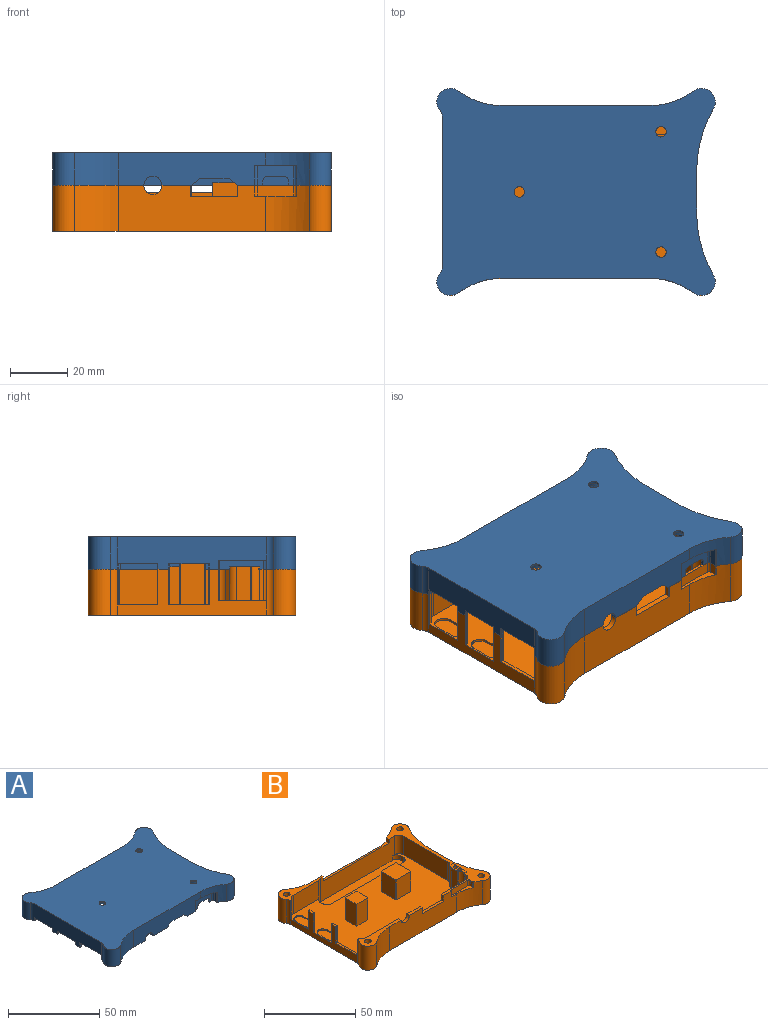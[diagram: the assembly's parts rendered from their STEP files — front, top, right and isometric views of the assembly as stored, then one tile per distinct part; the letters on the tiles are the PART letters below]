
ASSEMBLY  parts=2 mates=1
PART A: 96 faces, bbox 97.3x72.4x11.4 mm
  f0: cylinder r=1.6mm len=1.6mm, axis (0,-1,0), area 2.4mm2, adj f1,f2,f45,f55
  f1: plane 1.58x0.96mm, normal (1,0,0), area 1.5mm2, adj f0,f45,f55,f72
  f2: plane 5.69x0.96mm, normal (0,0,-1), area 5.5mm2, adj f0,f45,f47,f55
  f3: plane 11.74x2.84mm, normal (1,0,0), area 33.4mm2, adj f6,f8,f11,f71
  f4: plane 11.49x2.84mm, normal (0,-1,0), area 32.7mm2, adj f5,f6,f8,f71
  f5: cylinder r=0.25mm len=2.85mm, axis (0,0,1), area 1.1mm2, adj f4,f6,f7,f71
  f6: plane 12.25x12mm, normal (0,0,-1), area 146.9mm2, adj f3,f4,f5,f7,f8,f9,f10,f11
  f7: plane 11.74x2.84mm, normal (-1,0,0), area 33.4mm2, adj f5,f6,f9,f71
  f8: cylinder r=0.25mm len=2.85mm, axis (0,0,1), area 1.1mm2, adj f3,f4,f6,f71
  f9: cylinder r=0.25mm len=2.85mm, axis (0,0,1), area 1.1mm2, adj f6,f7,f10,f71
  f10: plane 11.49x2.84mm, normal (0,1,0), area 32.7mm2, adj f6,f9,f11,f71
  f11: cylinder r=0.25mm len=2.85mm, axis (0,0,1), area 1.1mm2, adj f3,f6,f10,f71
  f12: cylinder r=0.25mm len=2.03mm, axis (0,0,1), area 0.8mm2, adj f19,f57,f94,f95
  f13: cylinder r=0.23mm len=2.03mm, axis (0,0,-1), area 0.6mm2, adj f19,f43,f69,f70
  f14: cylinder r=3.43mm len=11.43mm, axis (0,0,-1), area 27.9mm2, adj f20,f25,f38,f70,f92
  f15: plane 16.88x1.44mm, normal (0,0,-1), area 19.7mm2, adj f16,f17,f18,f37,f44,f57,f66,f67
  f16: cylinder r=0.25mm len=3.23mm, axis (0,0,1), area 1.3mm2, adj f15,f17,f57,f65
  f17: plane 3.23x0.69mm, normal (0,-1,0), area 2.2mm2, adj f15,f16,f18,f65
  f18: cylinder r=0.25mm len=3.23mm, axis (0,0,1), area 1.3mm2, adj f15,f17,f65,f92
  f19: plane 14.2x1.4mm, normal (0,0,-1), area 16.5mm2, adj f12,f13,f20,f43,f57,f69,f92,f93
  f20: cylinder r=0.23mm len=2.03mm, axis (0,0,-1), area 0.7mm2, adj f14,f19,f69,f70
  f21: cylinder r=1.83mm len=3.66mm, axis (0,0,1), area 9mm2, adj f24,f38
  f22: cylinder r=1.83mm len=3.66mm, axis (0,0,1), area 9mm2, adj f23,f38
  f23: cone r=1.83mm half-angle=41deg, axis (0,0,-1), area 63.9mm2, adj f22,f71
  f24: cone r=1.77mm half-angle=41deg, axis (0,0,-1), area 63.9mm2, adj f21,f71
  f25: cylinder r=4.76mm len=11.43mm, axis (0,0,-1), area 159.2mm2, adj f14,f26,f38,f70
  f26: cylinder r=25.4mm len=15.24mm, axis (0,0,-1), area 186.8mm2, adj f25,f27,f38,f70
  f27: plane 51.56x11.43mm, normal (0,1,0), area 589.4mm2, adj f26,f28,f38,f70
  f28: cylinder r=25.4mm len=15.24mm, axis (0,0,-1), area 186.8mm2, adj f27,f29,f38,f70
  f29: cylinder r=4.76mm len=11.43mm, axis (0,0,-1), area 148.8mm2, adj f28,f30,f38,f70
  f30: cylinder r=44.45mm len=22.05mm, axis (0,0,-1), area 263.7mm2, adj f29,f31,f38,f70
  f31: plane 14.04x11.43mm, normal (1,0,0), area 140.5mm2, adj f30,f32,f38,f70,f80,f81,f82,f83
  f32: cylinder r=44.45mm len=22.05mm, axis (0,0,-1), area 263.7mm2, adj f31,f33,f38,f70
  f33: cylinder r=4.76mm len=11.43mm, axis (0,0,-1), area 148.8mm2, adj f32,f34,f38,f70
  f34: cylinder r=25.4mm len=15.24mm, axis (0,0,-1), area 108.6mm2, adj f33,f38,f46,f51,f52,f70
  f35: cylinder r=25.4mm len=15.24mm, axis (0,0,-1), area 186.8mm2, adj f36,f38,f46,f49
  f36: cylinder r=4.76mm len=11.43mm, axis (0,0,-1), area 159.2mm2, adj f35,f37,f38,f49
  f37: cylinder r=3.43mm len=11.43mm, axis (0,0,-1), area 27.5mm2, adj f15,f36,f38,f49,f66,f92
  f38: plane 97.28x72.39mm, normal (0,0,1), area 5689.1mm2, adj f14,f21,f22,f25,f26,f27,f28,f29
  f39: cylinder r=3.43mm len=8.05mm, axis (0,0,1), area 43.4mm2, adj f40,f45,f70,f71
  f40: plane 49.66x8.05mm, normal (-1,0,0), area 379.9mm2, adj f39,f41,f70,f71,f80,f81,f82,f83
  f41: cylinder r=3.43mm len=8.05mm, axis (0,0,1), area 43.4mm2, adj f40,f42,f70,f71
  f42: plane 78.74x8.05mm, normal (0,-1,0), area 634mm2, adj f41,f43,f70,f71
  f43: cylinder r=3.43mm len=8.05mm, axis (0,0,1), area 40.9mm2, adj f13,f19,f42,f57,f70,f71
  f44: cylinder r=3.43mm len=8.05mm, axis (0,0,1), area 39.2mm2, adj f15,f45,f49,f57,f68,f71
  f45: plane 78.74x8.05mm, normal (0,1,0), area 558.8mm2, adj f0,f1,f2,f39,f44,f47,f48,f49
  f46: plane 51.56x11.43mm, normal (0,-1,0), area 513.2mm2, adj f34,f35,f38,f49,f50,f51,f72,f73
  f47: cylinder r=1.6mm len=1.6mm, axis (0,-1,0), area 2.4mm2, adj f2,f45,f48,f55
  f48: plane 1.58x0.96mm, normal (-1,0,0), area 1.5mm2, adj f45,f47,f55,f70
  f49: plane 31.8x10.25mm, normal (0,0,-1), area 122.7mm2, adj f35,f36,f37,f44,f45,f46,f66,f67
  f50: cylinder r=0.25mm len=6.99mm, axis (0,0,1), area 2.5mm2, adj f46,f51,f56,f72
  f51: plane 14.86x3.37mm, normal (0,0,-1), area 21.6mm2, adj f34,f46,f50,f52,f53,f54,f55,f56
  f52: cylinder r=0.25mm len=6.99mm, axis (0,0,1), area 2mm2, adj f34,f51,f53,f70
  f53: plane 6.99x2.25mm, normal (-1,0,0), area 15.7mm2, adj f51,f52,f54,f70
  f54: cylinder r=0.89mm len=6.99mm, axis (0,0,1), area 9.8mm2, adj f51,f53,f55,f70
  f55: plane 12.7x6.99mm, normal (0,-1,0), area 61.6mm2, adj f0,f1,f2,f47,f48,f51,f54,f56
  f56: cylinder r=0.89mm len=6.99mm, axis (0,0,1), area 8.7mm2, adj f50,f51,f55,f72
  f57: plane 49.66x8.05mm, normal (1,0,0), area 294.6mm2, adj f12,f15,f16,f19,f43,f44,f60,f61
  f58: cylinder r=0.25mm len=2.03mm, axis (0,0,1), area 0.8mm2, adj f59,f61,f65,f92
  f59: plane 2.03x0.69mm, normal (0,1,0), area 1.4mm2, adj f58,f60,f61,f65
  f60: cylinder r=0.25mm len=2.03mm, axis (0,0,1), area 0.8mm2, adj f57,f59,f61,f65
  f61: plane 14.22x1.19mm, normal (0,0,-1), area 16.4mm2, adj f57,f58,f59,f60,f62,f63,f64,f92
  f62: cylinder r=0.25mm len=2.03mm, axis (0,0,1), area 0.8mm2, adj f57,f61,f63,f95
  f63: plane 2.03x0.69mm, normal (0,-1,0), area 1.4mm2, adj f61,f62,f64,f95
  f64: cylinder r=0.25mm len=2.03mm, axis (0,0,1), area 0.8mm2, adj f61,f63,f92,f95
  f65: plane 3.7x1.19mm, normal (0,0,-1), area 4.4mm2, adj f16,f17,f18,f57,f58,f59,f60,f92
  f66: cylinder r=0.25mm len=3.23mm, axis (0,0,1), area 1.3mm2, adj f15,f37,f49,f67
  f67: plane 3.23x0.95mm, normal (0,1,0), area 3.1mm2, adj f15,f49,f66,f68
  f68: cylinder r=0.25mm len=3.23mm, axis (0,0,1), area 1mm2, adj f15,f44,f49,f67
  f69: plane 2.03x0.96mm, normal (0,-1,0), area 1.9mm2, adj f13,f19,f20,f70
  f70: plane 97.28x72.39mm, normal (0,0,-1), area 572.3mm2, adj f13,f14,f20,f25,f26,f27,f28,f29
  f71: plane 85.6x56.52mm, normal (0,0,-1), area 4523.3mm2, adj f3,f4,f5,f7,f8,f9,f10,f11
  f72: plane 9.02x1.91mm, normal (0,0,-1), area 14.7mm2, adj f1,f45,f46,f50,f55,f56,f75
  f73: cylinder r=3.17mm len=6.35mm, axis (0,1,0), area 19mm2, adj f45,f46,f49,f74
  f74: plane 10.39x1.91mm, normal (0,0,-1), area 19.8mm2, adj f45,f46,f73,f77
  f75: plane 3.18x2.54mm, normal (-0.62,0,-0.78), area 7.7mm2, adj f45,f46,f72,f76
  f76: plane 9.53x1.91mm, normal (0,0,-1), area 18.1mm2, adj f45,f46,f75,f77
  f77: plane 3.18x2.54mm, normal (0.62,0,-0.78), area 7.7mm2, adj f45,f46,f74,f76
  f78: cylinder r=1.83mm len=3.66mm, axis (0,0,1), area 9mm2, adj f38,f79
  f79: cone r=1.83mm half-angle=41deg, axis (0,0,-1), area 63.9mm2, adj f71,f78
  f80: cylinder r=0.81mm len=2.03mm, axis (1,0,0), area 5.2mm2, adj f31,f40,f81,f83
  f81: plane 11x2.03mm, normal (0,0,-1), area 22.3mm2, adj f31,f40,f80,f82
  f82: cylinder r=0.81mm len=2.03mm, axis (1,0,0), area 5.2mm2, adj f31,f40,f81,f83
  f83: plane 11x2.03mm, normal (0,0,1), area 22.3mm2, adj f31,f40,f80,f82
  f84: cylinder r=1.52mm len=9.88mm, axis (0,0,1), area 94.6mm2, adj f49,f90
  f85: cylinder r=1.52mm len=9.88mm, axis (0,0,1), area 94.6mm2, adj f70,f91
  f86: cylinder r=1.52mm len=9.88mm, axis (0,0,1), area 94.6mm2, adj f70,f88
  f87: cylinder r=1.52mm len=9.88mm, axis (0,0,1), area 94.6mm2, adj f70,f89
  f88: cone r=0.8mm half-angle=59deg, axis (0,0,-1), area 8.5mm2, adj f86
  f89: cone r=0.8mm half-angle=59deg, axis (0,0,-1), area 8.5mm2, adj f87
  f90: cone r=0.8mm half-angle=59deg, axis (0,0,-1), area 8.5mm2, adj f84
  f91: cone r=0.8mm half-angle=59deg, axis (0,0,-1), area 8.5mm2, adj f85
  f92: plane 52.18x11.43mm, normal (-1,0,0), area 484.5mm2, adj f14,f15,f18,f19,f37,f38,f58,f61
  f93: cylinder r=0.25mm len=2.03mm, axis (0,0,-1), area 0.8mm2, adj f19,f92,f94,f95
  f94: plane 2.03x0.69mm, normal (0,1,0), area 1.4mm2, adj f12,f19,f93,f95
  f95: plane 4.28x1.19mm, normal (0,0,-1), area 5.1mm2, adj f12,f57,f62,f63,f64,f92,f93,f94
PART B: 132 faces, bbox 97.3x72.4x18.3 mm
  f0: cylinder r=0.23mm len=12.45mm, axis (0,0,1), area 4.5mm2, adj f21,f36,f65,f92
  f1: cylinder r=0.25mm len=0.94mm, axis (0,0,-1), area 0.4mm2, adj f28,f41,f56,f83
  f2: cylinder r=3.43mm len=12.45mm, axis (0,0,-1), area 33.8mm2, adj f28,f36,f51,f101
  f3: plane 50.8x2.31mm, normal (0,0,1), area 70.5mm2, adj f9,f12,f24,f37,f127
  f4: cylinder r=3.17mm len=6.35mm, axis (0,-1,0), area 19mm2, adj f42,f43,f88,f105
  f5: cylinder r=0.25mm len=3.81mm, axis (0,0,-1), area 1.1mm2, adj f28,f29,f31,f81
  f6: cylinder r=0.25mm len=10.92mm, axis (0,0,-1), area 4.4mm2, adj f15,f66,f93,f94
  f7: cylinder r=0.25mm len=3.94mm, axis (0,0,1), area 1.6mm2, adj f43,f70,f96,f105
  f8: plane 6.86x0.76mm, normal (1,0,0), area 5.2mm2, adj f35,f36,f47,f86
  f9: cylinder r=25.4mm len=16.08mm, axis (0,0,1), area 244.9mm2, adj f3,f12,f28,f62,f85,f127
  f10: cylinder r=0.25mm len=3.81mm, axis (0,0,-1), area 1.3mm2, adj f11,f28,f29,f88
  f11: cylinder r=0.89mm len=3.81mm, axis (0,0,-1), area 4.7mm2, adj f10,f28,f29,f50
  f12: plane 51.56x16.08mm, normal (0,1,0), area 717.7mm2, adj f3,f9,f37,f85,f92,f126
  f13: plane 2.12x0.94mm, normal (0,1,0), area 2mm2, adj f28,f57,f83,f103
  f14: plane 52.18x16.08mm, normal (-1,0,0), area 301.9mm2, adj f36,f64,f65,f67,f69,f76,f85,f93
  f15: plane 18.72x12.45mm, normal (1,0,0), area 63.4mm2, adj f6,f23,f33,f36,f93,f94
  f16: cylinder r=4.76mm len=16.08mm, axis (0,0,1), area 209.3mm2, adj f28,f81,f85,f87
  f17: plane 12.45x0.69mm, normal (0,1,0), area 8.5mm2, adj f23,f36,f64,f93
  f18: cylinder r=0.89mm len=3.81mm, axis (0,0,-1), area 5.3mm2, adj f28,f29,f31,f50
  f19: plane 13.39x4.89mm, normal (-1,0,0), area 65.4mm2, adj f36,f52,f63,f83
  f20: cylinder r=3.43mm len=3.43mm, axis (0,0,-1), area 16.6mm2, adj f36,f38,f84,f129
  f21: plane 12.45x0.96mm, normal (0,-1,0), area 11.9mm2, adj f0,f36,f92,f131
  f22: plane 3.07x1.78mm, normal (-1,0,0), area 5.5mm2, adj f36,f38,f48,f49
  f23: cylinder r=0.25mm len=12.45mm, axis (0,0,-1), area 5mm2, adj f15,f17,f36,f93
  f24: plane 57.06x15.52mm, normal (0,-1,0), area 751.3mm2, adj f3,f28,f34,f36,f37,f38,f48,f92
  f25: cylinder r=0.25mm len=3.94mm, axis (0,0,-1), area 1.6mm2, adj f28,f68,f70,f88
  f26: cylinder r=3.43mm len=12.45mm, axis (0,0,-1), area 67mm2, adj f28,f36,f72,f105
  f27: cylinder r=0.25mm len=0.94mm, axis (0,0,-1), area 0.4mm2, adj f28,f41,f83,f102
  f28: plane 72.39x32.87mm, normal (0,0,1), area 376.6mm2, adj f1,f2,f5,f9,f10,f11,f13,f16
  f29: plane 14.86x3.37mm, normal (0,0,1), area 21.6mm2, adj f5,f10,f11,f18,f31,f50,f81,f88
  f30: cylinder r=44.45mm len=22.05mm, axis (0,0,1), area 371mm2, adj f28,f62,f71,f85
  f31: plane 3.81x2.25mm, normal (-1,0,0), area 8.6mm2, adj f5,f18,f28,f29
  f32: cylinder r=1.83mm len=13.48mm, axis (0,0,-1), area 154.9mm2, adj f42,f90
  f33: cylinder r=3.43mm len=12.45mm, axis (0,0,1), area 53mm2, adj f15,f36,f42,f94,f95,f105
  f34: cylinder r=3.43mm len=12.45mm, axis (0,0,1), area 67mm2, adj f24,f28,f36,f51
  f35: cylinder r=3.17mm len=6.35mm, axis (0,0,-1), area 7.6mm2, adj f8,f36,f47,f55
  f36: plane 86.79x57.08mm, normal (0,0,1), area 3958.8mm2, adj f0,f2,f8,f14,f15,f17,f19,f20
  f37: plane 2.54x1.34mm, normal (1,0,0), area 3.4mm2, adj f3,f12,f24,f92
  f38: plane 62.23x8.64mm, normal (0,0,1), area 527.3mm2, adj f20,f22,f24,f48,f49,f84,f129,f130
  f39: plane 10.92x1.07mm, normal (0,1,0), area 11.7mm2, adj f42,f78,f94,f95
  f40: plane 12.45x3.78mm, normal (1,0,0), area 47mm2, adj f36,f59,f98,f100
  f41: plane 1.18x0.94mm, normal (0,-1,0), area 1.1mm2, adj f1,f27,f28,f83
  f42: plane 31.8x10.25mm, normal (0,0,1), area 119.5mm2, adj f4,f32,f33,f39,f45,f69,f78,f80
  f43: plane 10.39x1.91mm, normal (0,0,1), area 19.8mm2, adj f4,f7,f77,f88,f96,f105
  f44: cylinder r=0.25mm len=3.94mm, axis (0,0,-1), area 1.6mm2, adj f28,f68,f70,f105
  f45: cylinder r=4.76mm len=16.08mm, axis (0,0,1), area 224mm2, adj f42,f69,f80,f85
  f46: cylinder r=1.1mm len=17.02mm, axis (0,0,1), area 118.1mm2, adj f83,f85
  f47: plane 13.21x6.35mm, normal (0,0,1), area 75.2mm2, adj f8,f35,f55,f86
  f48: cylinder r=3.43mm len=3.43mm, axis (0,0,-1), area 16.6mm2, adj f22,f24,f36,f38
  f49: cylinder r=3.43mm len=3.43mm, axis (0,0,-1), area 16.6mm2, adj f22,f36,f38,f129
  f50: plane 12.7x3.81mm, normal (0,-1,0), area 48.4mm2, adj f11,f18,f28,f29
  f51: plane 34.64x12.45mm, normal (-1,0,0), area 431.2mm2, adj f2,f28,f34,f36
  f52: cylinder r=3.43mm len=13.39mm, axis (0,0,-1), area 36.2mm2, adj f19,f28,f36,f57,f83,f101
  f53: plane 13.21x6.35mm, normal (0,0,1), area 75.2mm2, adj f54,f58,f74,f104
  f54: cylinder r=3.17mm len=6.35mm, axis (0,0,-1), area 7.6mm2, adj f36,f53,f58,f104
  f55: plane 6.86x0.76mm, normal (-1,0,0), area 5.2mm2, adj f35,f36,f47,f86
  f56: plane 9.97x0.94mm, normal (1,0,0), area 9.4mm2, adj f1,f28,f83,f103
  f57: cylinder r=0.25mm len=0.94mm, axis (0,0,-1), area 0.2mm2, adj f13,f28,f52,f83
  f58: plane 6.86x0.76mm, normal (1,0,0), area 5.2mm2, adj f36,f53,f54,f74
  f59: cylinder r=0.25mm len=12.45mm, axis (0,0,-1), area 5mm2, adj f36,f40,f97,f98
  f60: cylinder r=1.1mm len=17.02mm, axis (0,0,1), area 118.1mm2, adj f83,f85
  f61: cone r=1.83mm half-angle=41deg, axis (0,0,-1), area 63.9mm2, adj f85,f125
  f62: cylinder r=4.76mm len=16.08mm, axis (0,0,1), area 209.3mm2, adj f9,f28,f30,f85
  f63: cylinder r=0.25mm len=13.39mm, axis (0,0,-1), area 3.5mm2, adj f19,f36,f83,f102
  f64: cylinder r=0.25mm len=12.45mm, axis (0,0,-1), area 5mm2, adj f14,f17,f36,f93
  f65: cylinder r=3.43mm len=16.08mm, axis (0,0,1), area 39.2mm2, adj f0,f14,f75,f85,f92
  f66: plane 10.92x0.69mm, normal (0,-1,0), area 7.5mm2, adj f6,f67,f93,f94
  f67: cylinder r=0.25mm len=10.92mm, axis (0,0,-1), area 4.4mm2, adj f14,f66,f93,f94
  f68: plane 3.94x1.4mm, normal (-1,0,0), area 5.5mm2, adj f25,f28,f44,f70
  f69: cylinder r=3.43mm len=16.08mm, axis (0,0,1), area 39.1mm2, adj f14,f42,f45,f78,f85
  f70: plane 16.38x1.91mm, normal (0,0,1), area 30.3mm2, adj f7,f25,f44,f68,f77,f88,f96,f105
  f71: plane 16.08x14.04mm, normal (1,0,0), area 225.7mm2, adj f28,f30,f85,f87
  f72: plane 12.45x1.22mm, normal (-1,0,0), area 15.2mm2, adj f26,f28,f36,f102
  f73: cylinder r=3.43mm len=12.45mm, axis (0,0,-1), area 52.1mm2, adj f36,f92,f128,f131
  f74: cylinder r=3.17mm len=6.35mm, axis (0,0,-1), area 7.6mm2, adj f36,f53,f58,f104
  f75: cylinder r=4.76mm len=16.08mm, axis (0,0,1), area 224mm2, adj f65,f85,f92,f126
  f76: cylinder r=0.25mm len=12.45mm, axis (0,0,-1), area 5mm2, adj f14,f36,f97,f98
  f77: cylinder r=0.25mm len=3.94mm, axis (0,0,1), area 1.6mm2, adj f43,f70,f88,f96
  f78: cylinder r=0.15mm len=10.92mm, axis (0,0,-1), area 2.6mm2, adj f39,f42,f69,f94
  f79: cylinder r=1.83mm len=13.48mm, axis (0,0,-1), area 154.9mm2, adj f28,f124
  f80: cylinder r=25.4mm len=16.08mm, axis (0,0,1), area 262.8mm2, adj f42,f45,f85,f88
  f81: cylinder r=25.4mm len=16.08mm, axis (0,0,1), area 220.1mm2, adj f5,f16,f28,f29,f85,f88
  f82: plane 12.45x0.69mm, normal (0,1,0), area 8.5mm2, adj f36,f98,f99,f100
  f83: plane 10.48x3.48mm, normal (0,0,1), area 24.2mm2, adj f1,f13,f19,f27,f41,f46,f52,f56
  f84: plane 3.07x1.78mm, normal (1,0,0), area 5.5mm2, adj f20,f36,f38,f130
  f85: plane 97.28x72.39mm, normal (0,0,-1), area 5503.1mm2, adj f9,f12,f14,f16,f30,f45,f46,f60
  f86: cylinder r=3.17mm len=6.35mm, axis (0,0,-1), area 7.6mm2, adj f8,f36,f47,f55
  f87: cylinder r=44.45mm len=22.05mm, axis (0,0,1), area 371mm2, adj f16,f28,f71,f85
  f88: plane 51.56x16.08mm, normal (0,-1,0), area 733.4mm2, adj f4,f10,f25,f28,f29,f42,f43,f70
  f89: cylinder r=1.83mm len=13.48mm, axis (0,0,-1), area 154.9mm2, adj f91,f92
  f90: cone r=1.83mm half-angle=41deg, axis (0,0,-1), area 63.9mm2, adj f32,f85
  f91: cone r=1.83mm half-angle=41deg, axis (0,0,-1), area 64.1mm2, adj f85,f89
  f92: plane 30.57x10.34mm, normal (0,0,1), area 115.3mm2, adj f0,f12,f21,f24,f37,f65,f73,f75
  f93: plane 3.7x1.19mm, normal (0,0,1), area 4.4mm2, adj f6,f14,f15,f17,f23,f64,f66,f67
  f94: plane 16.79x1.43mm, normal (0,0,1), area 19.7mm2, adj f6,f14,f15,f33,f39,f66,f67,f78
  f95: cylinder r=0.23mm len=10.92mm, axis (0,0,1), area 3mm2, adj f33,f39,f42,f94
  f96: plane 3.94x1.4mm, normal (1,0,0), area 5.5mm2, adj f7,f43,f70,f77
  f97: plane 12.45x0.69mm, normal (0,-1,0), area 8.5mm2, adj f36,f59,f76,f98
  f98: plane 4.28x1.19mm, normal (0,0,1), area 5.1mm2, adj f14,f40,f59,f76,f82,f97,f99,f100
  f99: cylinder r=0.25mm len=12.45mm, axis (0,0,1), area 5mm2, adj f14,f36,f82,f98
  f100: cylinder r=0.25mm len=12.45mm, axis (0,0,-1), area 5mm2, adj f36,f40,f82,f98
  f101: plane 12.45x1.44mm, normal (-0.7,0.71,0), area 25.2mm2, adj f2,f28,f36,f52
  f102: cylinder r=3.43mm len=13.39mm, axis (0,0,-1), area 47.2mm2, adj f27,f28,f36,f63,f72,f83
  f103: cylinder r=0.25mm len=0.94mm, axis (0,0,-1), area 0.4mm2, adj f13,f28,f56,f83
  f104: plane 6.86x0.76mm, normal (-1,0,0), area 5.2mm2, adj f36,f53,f54,f74
  f105: plane 77.06x12.45mm, normal (0,1,0), area 878.7mm2, adj f4,f7,f26,f28,f33,f36,f42,f43
  f106: cylinder r=0.25mm len=14.66mm, axis (0,0,1), area 5.8mm2, adj f36,f107,f113,f114
  f107: plane 14.66x8.38mm, normal (0,-1,0), area 122.8mm2, adj f36,f106,f108,f114
  f108: cylinder r=0.25mm len=14.66mm, axis (0,0,1), area 5.8mm2, adj f36,f107,f109,f114
  f109: plane 14.66x8.38mm, normal (1,0,0), area 122.8mm2, adj f36,f108,f110,f114
  f110: cylinder r=0.25mm len=14.66mm, axis (0,0,1), area 5.8mm2, adj f36,f109,f111,f114
  f111: plane 14.66x8.38mm, normal (0,1,0), area 122.8mm2, adj f36,f110,f112,f114
  f112: cylinder r=0.25mm len=14.66mm, axis (0,0,1), area 5.8mm2, adj f36,f111,f113,f114
  f113: plane 14.66x8.38mm, normal (-1,0,0), area 122.8mm2, adj f36,f106,f112,f114
  f114: plane 8.89x8.89mm, normal (0,0,1), area 79mm2, adj f106,f107,f108,f109,f110,f111,f112,f113
  f115: plane 13.39x11.18mm, normal (0,-1,0), area 149.6mm2, adj f36,f116,f122,f123
  f116: cylinder r=0.25mm len=13.39mm, axis (0,0,1), area 5.3mm2, adj f36,f115,f117,f123
  f117: plane 13.39x11.18mm, normal (1,0,0), area 149.6mm2, adj f36,f116,f118,f123
  f118: cylinder r=0.25mm len=13.39mm, axis (0,0,1), area 5.3mm2, adj f36,f117,f119,f123
  f119: plane 13.39x11.18mm, normal (0,1,0), area 149.6mm2, adj f36,f118,f120,f123
  f120: cylinder r=0.25mm len=13.39mm, axis (0,0,1), area 5.3mm2, adj f36,f119,f121,f123
  f121: plane 13.39x11.18mm, normal (-1,0,0), area 149.6mm2, adj f36,f120,f122,f123
  f122: cylinder r=0.25mm len=13.39mm, axis (0,0,1), area 5.3mm2, adj f36,f115,f121,f123
  f123: plane 11.68x11.68mm, normal (0,0,1), area 136.5mm2, adj f115,f116,f117,f118,f119,f120,f121,f122
  f124: cone r=1.83mm half-angle=41deg, axis (0,0,-1), area 63.9mm2, adj f79,f85
  f125: cylinder r=1.83mm len=13.48mm, axis (0,0,-1), area 154.9mm2, adj f28,f61
  f126: cylinder r=25.4mm len=16.08mm, axis (0,0,1), area 262.8mm2, adj f12,f75,f85,f92
  f127: plane 2.54x2.31mm, normal (-1,0,0), area 5.9mm2, adj f3,f9,f24,f28
  f128: plane 19.81x12.45mm, normal (0,-1,0), area 246.5mm2, adj f36,f73,f92,f130
  f129: plane 55.37x3.07mm, normal (0,1,0), area 170.2mm2, adj f20,f36,f38,f49
  f130: cylinder r=3.43mm len=15.52mm, axis (0,0,-1), area 41.3mm2, adj f24,f36,f38,f84,f92,f128
  f131: cylinder r=0.23mm len=12.45mm, axis (0,0,1), area 3.5mm2, adj f21,f36,f73,f92
PLACE A t=(-49.11,32.78,22.17)mm
PLACE B at identity
MATE fastened A.f85 <-> B.f89  axis (0,0,-1) through (0,0,16.46)mm
